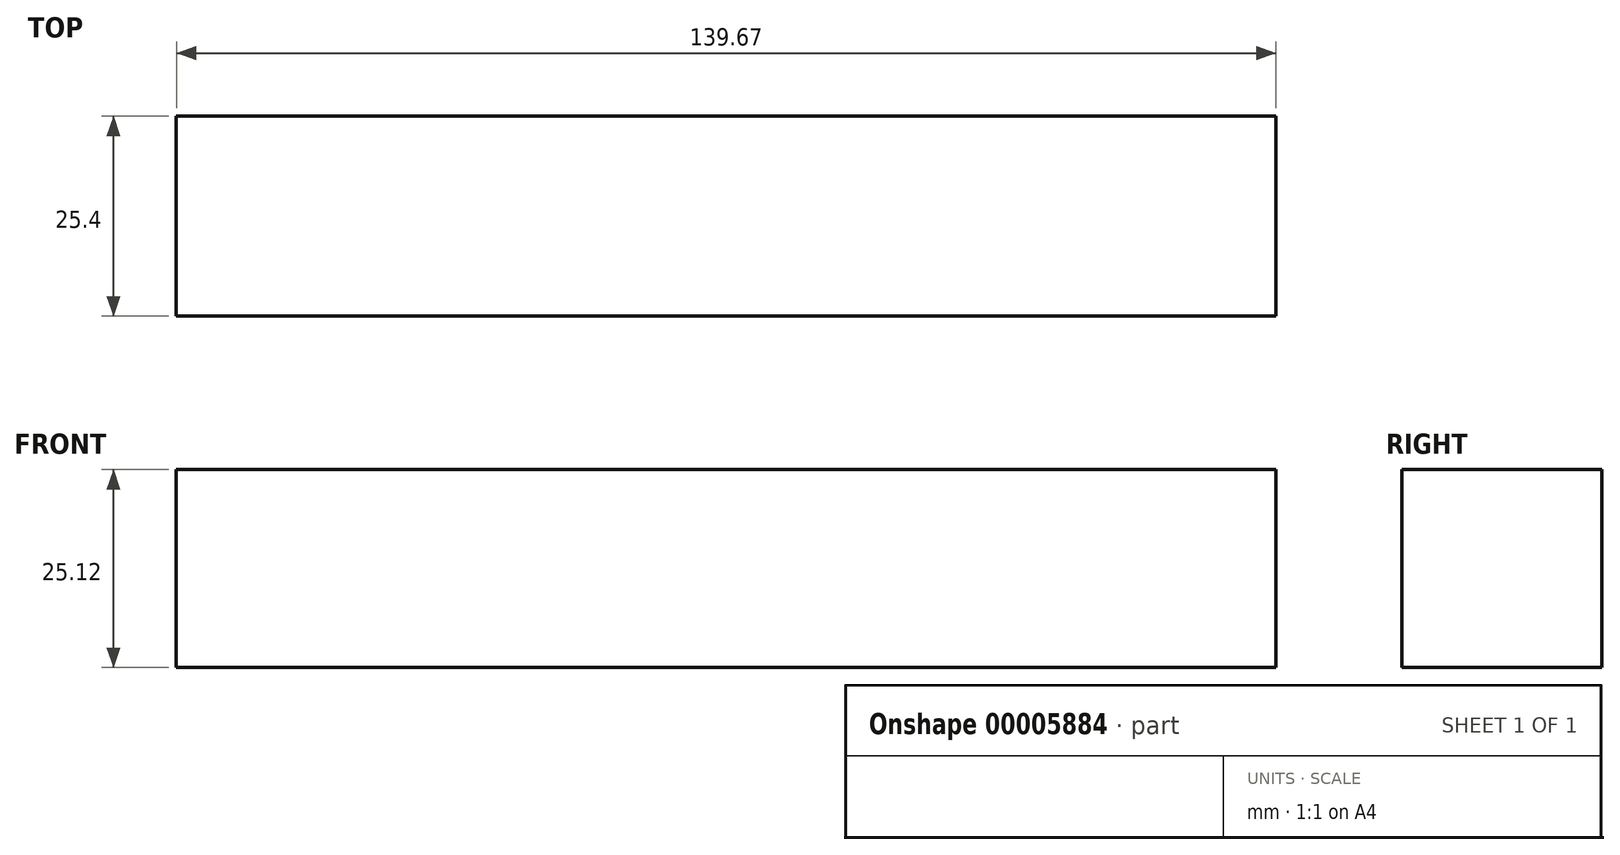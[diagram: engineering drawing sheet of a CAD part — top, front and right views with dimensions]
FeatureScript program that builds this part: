
annotation { "Feature Type Name" : "Feature", "Feature Type Description" : "" }
export const myFeature = defineFeature(function(context is Context, id is Id, definition is map)
    precondition{}
    {
        {
            var Q0;
            Q0=qCreatedBy(makeId("Front.planeOp"),FACE);
            var sketch = newSketch(context, id + "F0", { "sketchPlane" : qUnion([Q0])});
            skLineSegment(sketch, "E0.bottom", {"start": v(-67.92, -3.15) * mm, "end": v(71.75, -3.15) * mm});
            skLineSegment(sketch, "E0.top", {"start": v(-67.92, -28.27) * mm, "end": v(71.75, -28.27) * mm});
            skLineSegment(sketch, "E0.left", {"start": v(-67.92, -3.15) * mm, "end": v(-67.92, -28.27) * mm});
            skLineSegment(sketch, "E0.right", {"start": v(71.75, -3.15) * mm, "end": v(71.75, -28.27) * mm});
            skSolve(sketch);
        }
        {
            var Q0;
            Q0 = qSketchRegion(id + "F0", true);
            extrude(context, id + "F1", {"entities" : qUnion([Q0]), "depth" : 25.4 * mm});
        }
    });
